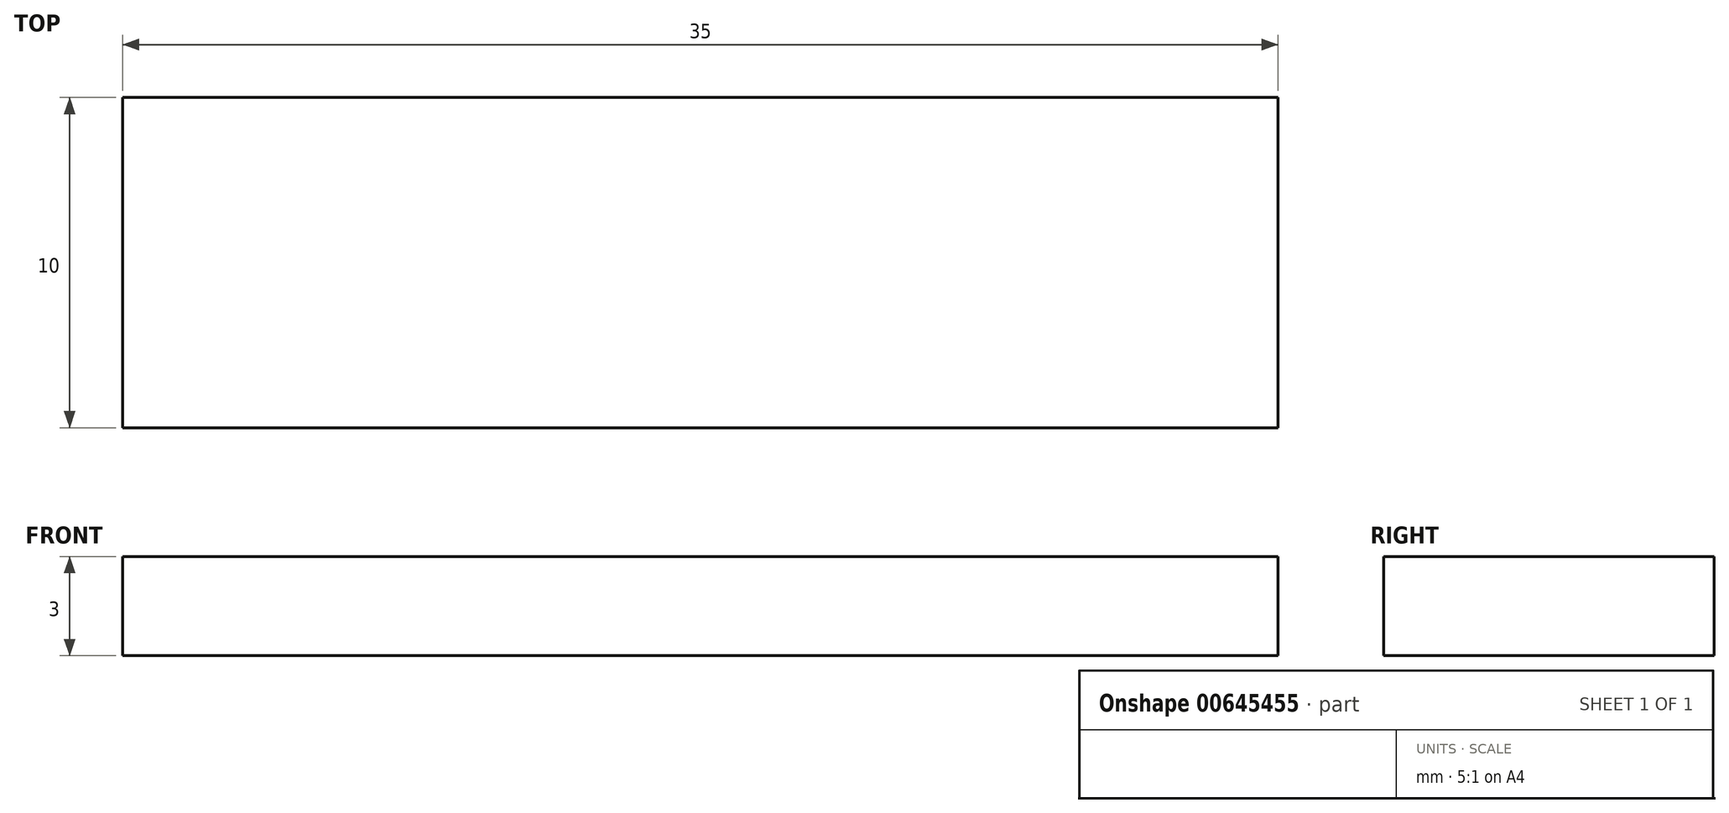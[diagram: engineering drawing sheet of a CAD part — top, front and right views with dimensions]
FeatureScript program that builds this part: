
annotation { "Feature Type Name" : "Feature", "Feature Type Description" : "" }
export const myFeature = defineFeature(function(context is Context, id is Id, definition is map)
    precondition{}
    {
        {
            var Q0;
            Q0=qCreatedBy(makeId("Top.planeOp"),FACE);
            var sketch = newSketch(context, id + "F0", { "sketchPlane" : qUnion([Q0])});
            skLineSegment(sketch, "E0.bottom", {"start": v(-17.5, 5) * mm, "end": v(17.5, 5) * mm});
            skLineSegment(sketch, "E0.top", {"start": v(-17.5, -5) * mm, "end": v(17.5, -5) * mm});
            skLineSegment(sketch, "E0.left", {"start": v(-17.5, 5) * mm, "end": v(-17.5, -5) * mm});
            skLineSegment(sketch, "E0.right", {"start": v(17.5, 5) * mm, "end": v(17.5, -5) * mm});
            skPoint(sketch, "E0.middle", {"position": v(0, 0) * mm});
            skSolve(sketch);
        }
        {
            var Q0;
            Q0 = qSketchRegion(id + "F0", true);
            extrude(context, id + "F1", {"entities" : qUnion([Q0]), "depth" : 3 * mm, "offsetDistance" : 25 * mm});
        }
    });
